# Revit family: Camera-Security-Panasonic-360-degree-Indoor-Dome-Network-S4150X
name_source: partatom
category: Security Devices
revit_build: Autodesk Revit 2016 (Build: 20150714_1515(x64)
units: mm (PartAtom-declared; Revit-internal decimal feet)

## family parameters
Cut with Voids When Loaded = No
Host = Face
Maintain Annotation Orientation = No
OmniClass Number = 23.85.10.14.11
OmniClass Title = Cameras
Part Type = Normal
Room Calculation Point = No
Round Connector Dimension = Use Diameter
Shared = No

## types (1)
- WV-S4150
    Alarm Input Or Output Specification = ALARM IN 1 (Auto time adjustment) (x1),ALARM IN 2 (ALARM OUT) (x1), ALARM IN 3 (AUX OUT) (x1)
    Angle Of View = 180
    Audio In = Yes
    Audio Out = Yes
    Communication Ports = 10Base-T / 100Base-TX, RJ45 connector
    Date Last Modified = November, 09, 2017
    Day Or Night = Yes
    Default Elevation = 0 "
    Description = Security Camera, 360-degree, Indoor, Dome, 5 Megapixel, Network, S4150
    Equipment Abbreviation = SC
    Family Version = 1.0.0
    Focal Length = 0.033 "
    Has POE = Yes
    Height_Offset5 = 1.447 "
    IP Or Analog = IP
    Indoor Or Outdoor = Indoor
    Manufacturer = Panasonic
    Minimum Illumination = 0 lx
    Model = WV-S4150
    Model Disclaimer = Contact Panasonic for more information
    Mounting Positions = Mount Dependent or Surface Mount
    Operational Humidity = 10% to 90% (no condensation)
    Part Description = Security Camera, 360-degree, Indoor, Dome, 5 Megapixel, Network, S4150
    Part Number = WV-S4150
    Power Active = 4.6 W
    Product Documentation Link = http://ssbu-t.psn-web.net
    Product Material = Paint - Panasonic - Sail White
    Product Page URL = https://security.panasonic.com
    Provide Feedback = https://www.surveymonkey.com
    Regulatory Compliance = UL UL60950-1, C-UL CAN/CSA C22.2 No.60950-1, CE, IEC60950-1 FCC Part15 ClassA, ICES003 ClassA, EN55022 ClassB, EN55024
    Scanning Area H = 0.14 "
    Scanning Area V = 0.14 "
    Storage Temperature = -22 °F to 140 °F
    URL = http://security.panasonic.com
    Vandal Resistant = No
    Voltage DC = 12 V
    Wide Dynamic Range = Yes
    z Base Height = 0 "
    z Base Raduius = 3.228 "
    z Horizontal FOV = 186.00°
    z Vertical FOV = 186.00°

## geometry (parser evidence)
native form markers: Blend x2, Sweep x4
no freeform markers — native parametric forms only
